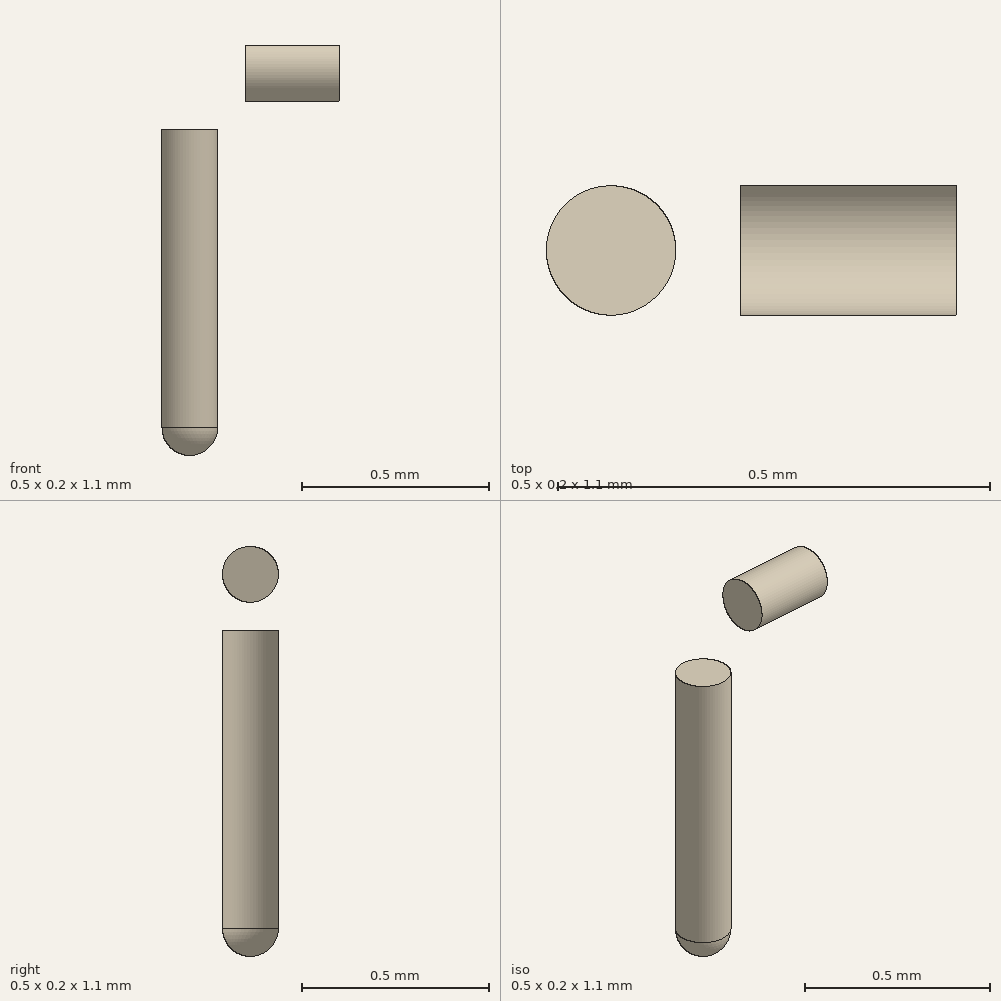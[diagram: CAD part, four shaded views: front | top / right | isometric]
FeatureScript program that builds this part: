
annotation { "Feature Type Name" : "Feature", "Feature Type Description" : "" }
export const myFeature = defineFeature(function(context is Context, id is Id, definition is map)
    precondition{}
    {
        {
            var Q0;
            Q0=qCreatedBy(makeId("Front.planeOp"),FACE);
            var sketch = newSketch(context, id + "F0", { "sketchPlane" : qUnion([Q0])});
            skLineSegment(sketch, "E0", {"start": v(0, 0) * mm, "end": v(0.07, 0) * mm});
            skLineSegment(sketch, "E1", {"start": v(0.07, 0) * mm, "end": v(0.07, -0.8) * mm});
            skLineSegment(sketch, "E2", {"start": v(0, 0) * mm, "end": v(0, -0.88) * mm});
            skArc(sketch, "E3", {"start": v(0, -0.87) * mm, "mid": v(0.05, -0.85) * mm, "end": v(0.07, -0.8) * mm});
            skSolve(sketch);
        }
        {
            var Q0;
            Q0=makeQuery(id+"F0.imprint","IMPRINT",FACE,{"disambiguationData":[TD([[makeQuery(id+"F0.imprint","IMPRINT",EDGE,{"derivedFrom":sQuery(id+"F0.wireOp",EDGE,"E0")}),-1.0]])]});
            var Q1;
            Q1=sQuery(id+"F0.wireOp",EDGE,"E2");
            revolve(context, id + "F1", {"entities" : qUnion([Q0]), "axis" : qUnion([Q1]), "revolveType" : RevolveType.FULL});
        }
        {
            var Q0;
            Q0=qCreatedBy(makeId("Front.planeOp"),FACE);
            var sketch = newSketch(context, id + "F2", { "sketchPlane" : qUnion([Q0])});
            skPoint(sketch, "E4", {"position": v(0.15, 0.15) * mm});
            skArc(sketch, "E5", {"start": v(0.15, 0.08) * mm, "mid": v(0.1, 0.05) * mm, "end": v(0.08, 0) * mm});
            skArc(sketch, "E6", {"start": v(0.15, 0.23) * mm, "mid": v(0, 0.16) * mm, "end": v(-0.07, 0) * mm});
            skSolve(sketch);
        }
        {
            var Q0;
            Q0=qCreatedBy(makeId("Right.planeOp"),FACE);
            cPlane(context, id + "F3", {"entities" : qUnion([Q0]), "cplaneType" : CPlaneType.OFFSET, "offset" : 0.15 * mm, "width" : 150 * mm, "height" : 150 * mm});
        }
        {
            var Q0;
            Q0=qCreatedBy(id+"F3.planeOp",FACE);
            var sketch = newSketch(context, id + "F4", { "sketchPlane" : qUnion([Q0])});
            skCircle(sketch, "E7", {"center": v(0, 0.15) * mm, "radius": 0.07 * mm});
            skSolve(sketch);
        }
        {
            var Q0;
            Q0 = qSketchRegion(id + "F4", true);
            extrude(context, id + "F5", {"entities" : qUnion([Q0]), "depth" : 0.25 * mm});
        }
        {
            var Q0;
            Q0=qCreatedBy(makeId("Front.planeOp"),FACE);
            cPlane(context, id + "F6", {"entities" : qUnion([Q0]), "cplaneType" : CPlaneType.OFFSET, "offset" : 0.07 * mm, "width" : 150 * mm, "height" : 150 * mm});
        }
        {
            var Q0;
            Q0=qCreatedBy(id+"F6.planeOp",FACE);
            var sketch = newSketch(context, id + "F7", { "sketchPlane" : qUnion([Q0])});
            skPoint(sketch, "E8", {"position": v(0, 0) * mm});
            skPoint(sketch, "E9", {"position": v(0.15, 0.15) * mm});
            skArc(sketch, "E10", {"start": v(0.15, 0.15) * mm, "mid": v(0.04, 0.1) * mm, "end": v(0, 0) * mm});
            skSolve(sketch);
        }
        {
            var Q0;
            Q0=qCreatedBy(makeId("Front.planeOp"),FACE);
            cPlane(context, id + "F8", {"entities" : qUnion([Q0]), "cplaneType" : CPlaneType.OFFSET, "offset" : 0.07 * mm, "oppositeDirection" : true, "width" : 150 * mm, "height" : 150 * mm});
        }
        {
            var Q0;
            Q0=makeQuery(id+"F1.opRevolve","SWEPT_FACE",FACE,{"disambiguationData":[OSD([sQuery(id+"F0.wireOp",EDGE,"E0")])]});
            var Q1;
            Q1=makeQuery(id+"F5.opExtrude","CAP_EDGE",EDGE,{"disambiguationData":[OSD([sQuery(id+"F4.wireOp",EDGE,"E7")])],"isStart":true});
            var Q2;
            Q2=sQuery(id+"F7.wireOp",EDGE,"E10");
            loft(context, id + "F9", {"bodyType" : ToolBodyType.SURFACE, "addGuides" : true, "wireProfilesArray" : [{ "wireProfileEntities" : qUnion([Q0]) }, { "wireProfileEntities" : qUnion([Q1]) }], "guidesArray" : [{ "guideEntities" : qUnion([Q2]), "guideDerivativeType" : LoftGuideDerivativeType.DEFAULT, "guideDerivativeMagnitude" : 1 }]});
        }
    });
